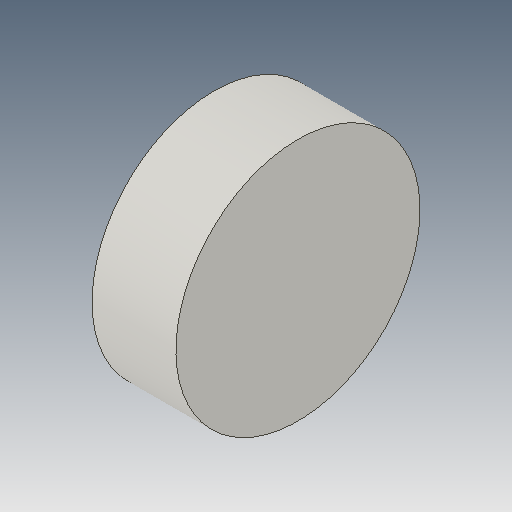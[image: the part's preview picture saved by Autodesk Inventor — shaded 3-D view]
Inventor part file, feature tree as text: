
AUTODESK INVENTOR PART (.ipt)
format: ipt  version: 2018 (Build 220112000, 112)  size: 83,456 bytes
history: native  units: in
note: dims shown in document units (in); Inventor stores cm internally (conversion verified against a paired STEP export)
features: other x3, sketch x1
ambient origin geometry x8: Origin, YZ Plane, XZ Plane, XY Plane, X Axis, Y Axis, Z Axis, Center Point
bodies: Solid1 (feature_tree)
feature tree (4):
  other  "Wheel.ipt"
  other  "Solid1::Wheel.ipt"
  other  "TaggingFeature1"
  sketch  "Sketch1"  dims[d0=0.3937in]
